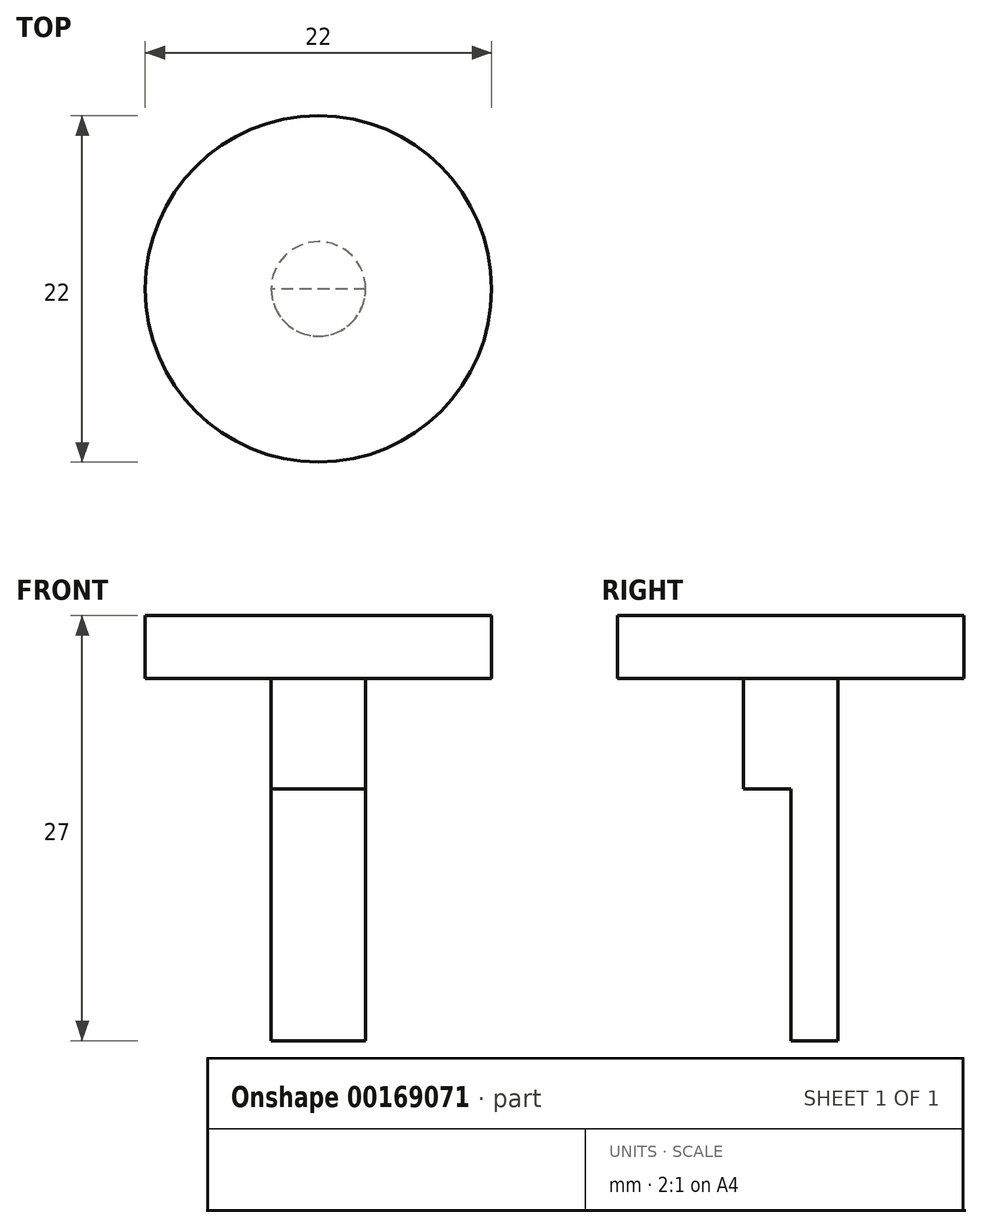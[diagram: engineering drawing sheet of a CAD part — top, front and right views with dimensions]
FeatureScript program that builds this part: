
annotation { "Feature Type Name" : "Feature", "Feature Type Description" : "" }
export const myFeature = defineFeature(function(context is Context, id is Id, definition is map)
    precondition{}
    {
        {
            var Q0;
            Q0=qCreatedBy(makeId("Front.planeOp"),FACE);
            var sketch = newSketch(context, id + "F0", { "sketchPlane" : qUnion([Q0])});
            skLineSegment(sketch, "E0.bottom", {"start": v(-3, 12.5) * mm, "end": v(3, 12.5) * mm});
            skLineSegment(sketch, "E0.top", {"start": v(-3, -12.5) * mm, "end": v(3, -12.5) * mm});
            skLineSegment(sketch, "E0.left", {"start": v(-3, 12.5) * mm, "end": v(-3, -12.5) * mm});
            skLineSegment(sketch, "E0.right", {"start": v(3, 12.5) * mm, "end": v(3, -12.5) * mm});
            skPoint(sketch, "E0.middle", {"position": v(0, 0) * mm});
            skLineSegment(sketch, "E1.bottom", {"start": v(-11, 14.5) * mm, "end": v(11, 14.5) * mm});
            skLineSegment(sketch, "E1.top", {"start": v(-11, 10.5) * mm, "end": v(11, 10.5) * mm});
            skLineSegment(sketch, "E1.left", {"start": v(-11, 14.5) * mm, "end": v(-11, 10.5) * mm});
            skLineSegment(sketch, "E1.right", {"start": v(11, 14.5) * mm, "end": v(11, 10.5) * mm});
            skPoint(sketch, "E1.middle", {"position": v(0, 12.5) * mm});
            skLineSegment(sketch, "E2", {"start": v(-3, 3.5) * mm, "end": v(3, 3.5) * mm});
            skLineSegment(sketch, "E3", {"start": v(0, 14.5) * mm, "end": v(0, -12.5) * mm});
            skSolve(sketch);
        }
        {
            var Q0;
            {var subQ0=sQuery(id+"F0.wireOp",EDGE,"E1.right");Q0=makeQuery(id+"F0.imprint","IMPRINT",FACE,{"disambiguationData":[TD([[makeQuery(id+"F0.imprint","IMPRINT",EDGE,{"derivedFrom":subQ0}),-1.0]])]});}
            var Q1;
            {var subQ0=sQuery(id+"F0.wireOp",EDGE,"E2");var subQ1=sQuery(id+"F0.wireOp",EDGE,"E0.right");var subQ2=makeQuery(id+"F0.imprint","INTERSECT",VERTEX,{"derivedFrom":[subQ1,subQ0]});Q1=makeQuery(id+"F0.imprint","IMPRINT",FACE,{"disambiguationData":[TD([[makeQuery(id+"F0.imprint","IMPRINT",EDGE,{"disambiguationData":[TD([[subQ2,1.0]])],"derivedFrom":subQ1}),-1.0]])]});}
            var Q2;
            {var subQ0=sQuery(id+"F0.wireOp",EDGE,"E0.right");var subQ1=sQuery(id+"F0.wireOp",EDGE,"E0.bottom");var subQ2=makeQuery(id+"F0.imprint","INTERSECT",VERTEX,{"derivedFrom":[subQ1,subQ0]});Q2=makeQuery(id+"F0.imprint","IMPRINT",FACE,{"disambiguationData":[TD([[makeQuery(id+"F0.imprint","IMPRINT",EDGE,{"disambiguationData":[TD([[subQ2,1.0]])],"derivedFrom":subQ1}),-1.0]])]});}
            var Q3;
            {var subQ0=sQuery(id+"F0.wireOp",EDGE,"E0.right");var subQ1=sQuery(id+"F0.wireOp",EDGE,"E0.top");var subQ2=makeQuery(id+"F0.imprint","INTERSECT",VERTEX,{"derivedFrom":[subQ1,subQ0]});Q3=makeQuery(id+"F0.imprint","IMPRINT",FACE,{"disambiguationData":[TD([[makeQuery(id+"F0.imprint","IMPRINT",EDGE,{"disambiguationData":[TD([[subQ2,1.0]])],"derivedFrom":subQ1}),1.0]])]});}
            var Q4;
            {var subQ0=sQuery(id+"F0.wireOp",EDGE,"0HZLNRYG-72Uo-OaGl-RmAj-lHV8erM4Oqk8");var subQ1=sQuery(id+"F0.wireOp",EDGE,"E0.right");var subQ2=makeQuery(id+"F0.imprint","INTERSECT",VERTEX,{"derivedFrom":[subQ1,subQ0]});Q4=makeQuery(id+"F0.imprint","IMPRINT",FACE,{"disambiguationData":[TD([[makeQuery(id+"F0.imprint","IMPRINT",EDGE,{"disambiguationData":[TD([[subQ2,1.0]])],"derivedFrom":subQ1}),-1.0]])]});}
            var Q5;
            Q5=sQuery(id+"F0.wireOp",EDGE,"E3");
            revolve(context, id + "F1", {"entities" : qUnion([Q0, Q1, Q2, Q3, Q4]), "axis" : qUnion([Q5]), "revolveType" : RevolveType.FULL});
        }
        {
            var Q0;
            {var subQ0=sQuery(id+"F0.wireOp",EDGE,"E0.left");var subQ1=sQuery(id+"F0.wireOp",EDGE,"E0.top");var subQ2=makeQuery(id+"F0.imprint","INTERSECT",VERTEX,{"derivedFrom":[subQ1,subQ0]});Q0=makeQuery(id+"F0.imprint","IMPRINT",FACE,{"disambiguationData":[TD([[makeQuery(id+"F0.imprint","IMPRINT",EDGE,{"disambiguationData":[TD([[subQ2,-1.0]])],"derivedFrom":subQ1}),1.0]])]});}
            var Q1;
            Q1=sQuery(id+"F0.wireOp",EDGE,"E3");
            revolve(context, id + "F2", {"operationType" : NewBodyOperationType.REMOVE, "entities" : qUnion([Q0]), "axis" : qUnion([Q1]), "revolveType" : RevolveType.ONE_DIRECTION, "oppositeDirection" : true, "angle" : 180 * degree});
        }
    });
